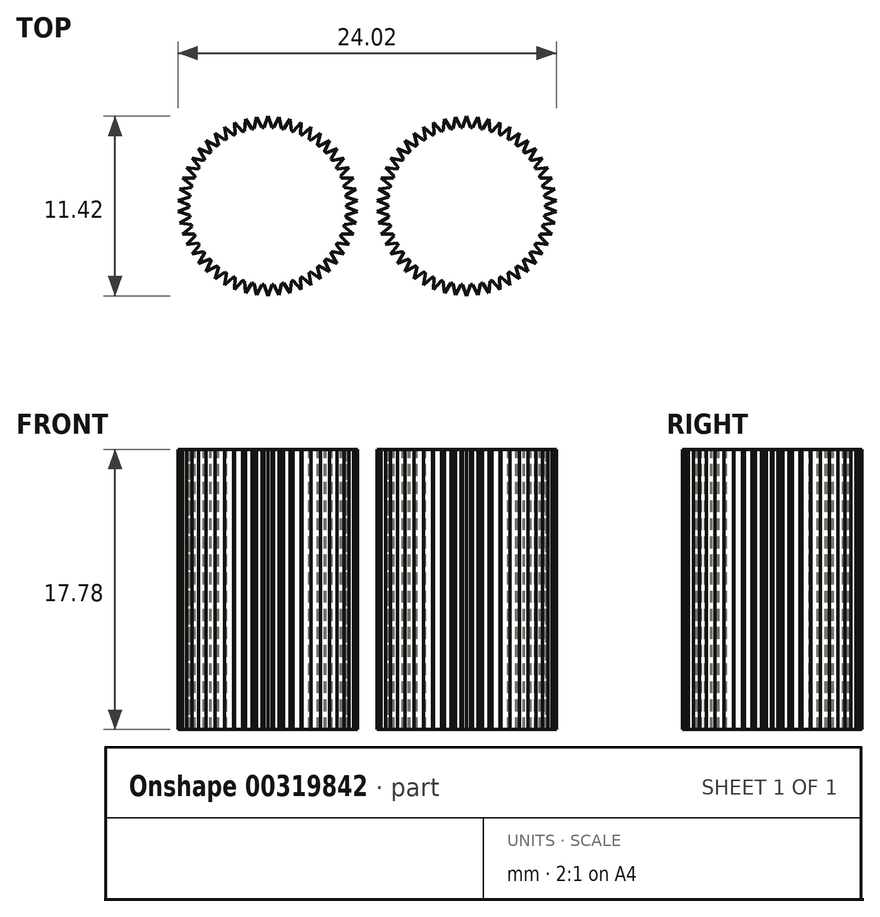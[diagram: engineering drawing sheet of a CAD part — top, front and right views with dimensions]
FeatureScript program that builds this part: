
annotation { "Feature Type Name" : "Feature", "Feature Type Description" : "" }
export const myFeature = defineFeature(function(context is Context, id is Id, definition is map)
    precondition{}
    {
        {
            var Q0;
            Q0=qCreatedBy(makeId("Top.planeOp"),FACE);
            var sketch = newSketch(context, id + "F0", { "sketchPlane" : qUnion([Q0])});
            skCircle(sketch, "E0", {"center": v(0, 0) * mm, "radius": 5 * mm});
            skSolve(sketch);
        }
        {
            var Q0;
            Q0 = qSketchRegion(id + "F0", true);
            extrude(context, id + "F1", {"entities" : qUnion([Q0]), "depth" : 17.78 * mm});
        }
        {
            var Q0;
            Q0=qCreatedBy(makeId("Top.planeOp"),FACE);
            var sketch = newSketch(context, id + "F2", { "sketchPlane" : qUnion([Q0])});
            skLineSegment(sketch, "E1", {"start": v(0, 5.71) * mm, "end": v(-0.25, 5) * mm});
            skLineSegment(sketch, "E2", {"start": v(-0.25, 5) * mm, "end": v(0.25, 5) * mm});
            skLineSegment(sketch, "E3", {"start": v(0.25, 5) * mm, "end": v(0, 5.71) * mm});
            skSolve(sketch);
        }
        {
            var Q0;
            Q0=makeQuery(id+"F1.opExtrude","CAP_FACE",FACE,{"disambiguationData":[OSD([sQuery(id+"F0.wireOp",EDGE,"E0")])],"isStart":false});
            var sketch = newSketch(context, id + "F3", { "sketchPlane" : qUnion([Q0])});
            skLineSegment(sketch, "E4", {"start": v(0, 5.71) * mm, "end": v(-0.25, 5) * mm});
            skLineSegment(sketch, "E5", {"start": v(-0.25, 5) * mm, "end": v(0.25, 5) * mm});
            skLineSegment(sketch, "E6", {"start": v(0.25, 5) * mm, "end": v(0, 5.71) * mm});
            skSolve(sketch);
        }
        {
            var Q1;
            Q1=makeQuery(id+"F2.imprint","IMPRINT",FACE,{"disambiguationData":[TD([[makeQuery(id+"F2.imprint","IMPRINT",EDGE,{"derivedFrom":sQuery(id+"F2.wireOp",EDGE,"E1")}),1.0]])]});
            var Q2;
            {var subQ0=sQuery(id+"F3.wireOp",EDGE,"E4");Q2=makeQuery(id+"F3.imprint","IMPRINT",FACE,{"disambiguationData":[TD([[makeQuery(id+"F3.imprint","IMPRINT",EDGE,{"derivedFrom":subQ0}),1.0]])]});}
            loft(context, id + "F4", {"sheetProfilesArray" : [{ "sheetProfileEntities" : qUnion([Q1]) }, { "sheetProfileEntities" : qUnion([Q2]) }]});
        }
        {
            var Q0;
            Q0=qCreatedBy(makeId("Front.planeOp"),FACE);
            var sketch = newSketch(context, id + "F5", { "sketchPlane" : qUnion([Q0])});
            skLineSegment(sketch, "E7", {"start": v(0, 7.95) * mm, "end": v(0, -3.36) * mm, "construction": true});
            skSolve(sketch);
        }
        {
            var Q0;
            {var subQ0=sQuery(id+"F3.wireOp",EDGE,"E4");Q0=makeQuery(id+"F4.opLoft","SWEPT_BODY",BODY,{"disambiguationData":[OSD([makeQuery(id+"F2.imprint","IMPRINT",FACE,{"disambiguationData":[TD([[makeQuery(id+"F2.imprint","IMPRINT",EDGE,{"derivedFrom":sQuery(id+"F2.wireOp",EDGE,"E1")}),1.0]])]}),makeQuery(id+"F3.imprint","IMPRINT",FACE,{"disambiguationData":[TD([[makeQuery(id+"F3.imprint","IMPRINT",EDGE,{"derivedFrom":subQ0}),1.0]])]})])]});}
            var Q1;
            Q1=sQuery(id+"F5.wireOp",EDGE,"E7");
            circularPattern(context, id + "F6", {"operationType" : NewBodyOperationType.ADD, "entities" : qUnion([Q0]), "axis" : qUnion([Q1]), "angle" : 360 * degree, "instanceCount" : 50, "equalSpace" : true});
        }
        {
            var Q0;
            Q0=makeQuery(id+"F1.opExtrude","SWEPT_BODY",BODY,{"disambiguationData":[OSD([sQuery(id+"F0.wireOp",EDGE,"E0")])]});
            transform(context, id + "F7", {"entities" : qUnion([Q0]), "transformType" : TransformType.TRANSLATION_3D, "dx" : 12.62 * mm, "dy" : 0 * mm, "dz" : 0 * mm, "makeCopy" : true});
        }
    });
